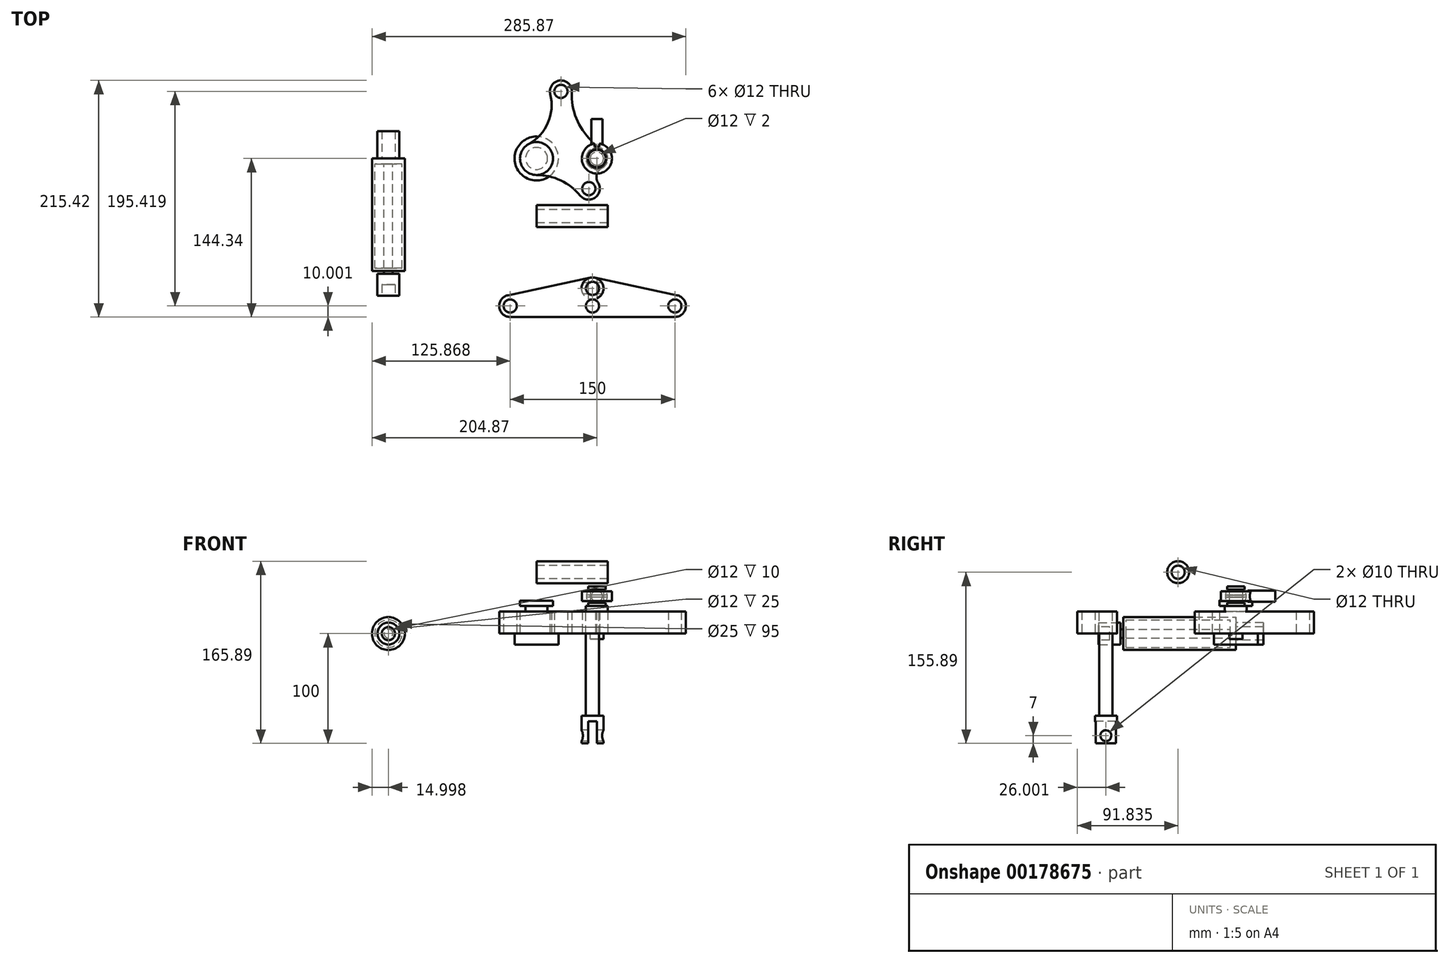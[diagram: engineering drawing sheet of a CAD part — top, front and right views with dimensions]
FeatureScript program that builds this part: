
annotation { "Feature Type Name" : "Feature", "Feature Type Description" : "" }
export const myFeature = defineFeature(function(context is Context, id is Id, definition is map)
    precondition{}
    {
        {
            var Q0;
            Q0=qCreatedBy(makeId("Top.planeOp"),FACE);
            var sketch = newSketch(context, id + "F0", { "sketchPlane" : qUnion([Q0])});
            skCircle(sketch, "E0", {"center": v(0, 0) * mm, "radius": 10 * mm});
            skCircle(sketch, "E1", {"center": v(55, 0) * mm, "radius": 6 * mm});
            skCircle(sketch, "E2", {"center": v(22.23, 61.08) * mm, "radius": 6 * mm});
            skCircle(sketch, "E3", {"center": v(22.23, 61.08) * mm, "radius": 10 * mm});
            skCircle(sketch, "E4", {"center": v(0, 0) * mm, "radius": 15 * mm});
            skCircle(sketch, "E5", {"center": v(55, 0) * mm, "radius": 10 * mm});
            skLineSegment(sketch, "E6", {"start": v(22.23, 61.08) * mm, "end": v(0, 0) * mm, "construction": true});
            skLineSegment(sketch, "E7", {"start": v(0, 0) * mm, "end": v(55, 0) * mm, "construction": true});
            skCircle(sketch, "E8", {"center": v(47.63, -27.5) * mm, "radius": 6 * mm});
            skCircle(sketch, "E9", {"center": v(47.63, -27.5) * mm, "radius": 10 * mm});
            skLineSegment(sketch, "E10", {"start": v(0, 0) * mm, "end": v(47.63, -27.5) * mm, "construction": true});
            skArc(sketch, "E11", {"start": v(-7.24, 13.14) * mm, "mid": v(10.4, 32.52) * mm, "end": v(12.54, 58.63) * mm});
            skArc(sketch, "E12", {"start": v(32.22, 60.57) * mm, "mid": v(38.92, 30.7) * mm, "end": v(60.1, 8.6) * mm});
            skArc(sketch, "E13", {"start": v(39.9, -33.85) * mm, "mid": v(22.07, -19.95) * mm, "end": v(0, -15) * mm});
            skArc(sketch, "E14", {"start": v(59.56, -8.9) * mm, "mid": v(54.87, -14.7) * mm, "end": v(56.03, -22.07) * mm});
            skSolve(sketch);
        }
        {
            var Q0;
            Q0 = qSketchRegion(id + "F0", true);
            extrude(context, id + "F1", {"entities" : qUnion([Q0]), "depth" : 20 * mm});
        }
        {
            var Q0;
            Q0=makeQuery(id+"F1.opExtrude","CAP_FACE",FACE,{"disambiguationData":[OSD([sQuery(id+"F0.wireOp",EDGE,"E0"),sQuery(id+"F0.wireOp",EDGE,"E1"),sQuery(id+"F0.wireOp",EDGE,"E2"),sQuery(id+"F0.wireOp",EDGE,"E3"),sQuery(id+"F0.wireOp",EDGE,"E4"),sQuery(id+"F0.wireOp",EDGE,"E5"),sQuery(id+"F0.wireOp",EDGE,"7eYs1WeX-2swm-OC1l-bZu6-TTdB08adliAf"),sQuery(id+"F0.wireOp",EDGE,"nQsTL9GD-XLsh-tJj3-fAuQ-5O212QxCRfNk"),sQuery(id+"F0.wireOp",EDGE,"hc34mphg-32rM-w2y4-HKMr-pzHpQo0iNHix")])],"isStart":true});
            var sketch = newSketch(context, id + "F2", { "sketchPlane" : qUnion([Q0])});
            skCircle(sketch, "E15", {"center": v(0, 0) * mm, "radius": 20 * mm});
            skSolve(sketch);
        }
        {
            var Q0;
            Q0 = qSketchRegion(id + "F2", true);
            extrude(context, id + "F3", {"entities" : qUnion([Q0]), "depth" : 10 * mm});
        }
        {
            var Q0;
            Q0=makeQuery(id+"F3.opExtrude","CAP_FACE",FACE,{"disambiguationData":[OSD([sQuery(id+"F2.wireOp",EDGE,"E15")])],"isStart":true});
            var sketch = newSketch(context, id + "F4", { "sketchPlane" : qUnion([Q0])});
            skCircle(sketch, "E16", {"center": v(0, 0) * mm, "radius": 10 * mm});
            skSolve(sketch);
        }
        {
            var Q0;
            Q0 = qSketchRegion(id + "F4", true);
            extrude(context, id + "F5", {"entities" : qUnion([Q0]), "operationType" : NewBodyOperationType.ADD, "depth" : 25 * mm});
        }
        {
            var Q0;
            Q0=makeQuery(id+"F5.opExtrude","CAP_FACE",FACE,{"disambiguationData":[OSD([sQuery(id+"F4.wireOp",EDGE,"E16")])],"isStart":false});
            var sketch = newSketch(context, id + "F6", { "sketchPlane" : qUnion([Q0])});
            skCircle(sketch, "E17", {"center": v(0, 0) * mm, "radius": 15 * mm});
            skSolve(sketch);
        }
        {
            var Q0;
            Q0 = qSketchRegion(id + "F6", true);
            extrude(context, id + "F7", {"entities" : qUnion([Q0]), "operationType" : NewBodyOperationType.ADD, "depth" : 5 * mm});
        }
        {
            var Q0;
            Q0=makeQuery(id+"F1.opExtrude","CAP_FACE",FACE,{"disambiguationData":[OSD([sQuery(id+"F0.wireOp",EDGE,"E0"),sQuery(id+"F0.wireOp",EDGE,"E1"),sQuery(id+"F0.wireOp",EDGE,"E2"),sQuery(id+"F0.wireOp",EDGE,"E3"),sQuery(id+"F0.wireOp",EDGE,"E4"),sQuery(id+"F0.wireOp",EDGE,"E5"),sQuery(id+"F0.wireOp",EDGE,"7eYs1WeX-2swm-OC1l-bZu6-TTdB08adliAf"),sQuery(id+"F0.wireOp",EDGE,"nQsTL9GD-XLsh-tJj3-fAuQ-5O212QxCRfNk"),sQuery(id+"F0.wireOp",EDGE,"hc34mphg-32rM-w2y4-HKMr-pzHpQo0iNHix")])],"isStart":false});
            var sketch = newSketch(context, id + "F8", { "sketchPlane" : qUnion([Q0])});
            skCircle(sketch, "E18", {"center": v(55, 0) * mm, "radius": 10 * mm});
            skSolve(sketch);
        }
        {
            var Q0;
            Q0 = qSketchRegion(id + "F8", true);
            extrude(context, id + "F9", {"entities" : qUnion([Q0]), "depth" : 5 * mm});
        }
        {
            var Q0;
            Q0=makeQuery(id+"F9.opExtrude","CAP_FACE",FACE,{"disambiguationData":[OSD([sQuery(id+"F8.wireOp",EDGE,"E18")])],"isStart":false});
            var sketch = newSketch(context, id + "F10", { "sketchPlane" : qUnion([Q0])});
            skCircle(sketch, "E19", {"center": v(55, 0) * mm, "radius": 8 * mm});
            skSolve(sketch);
        }
        {
            var Q0;
            Q0 = qSketchRegion(id + "F10", true);
            extrude(context, id + "F11", {"entities" : qUnion([Q0]), "operationType" : NewBodyOperationType.ADD, "depth" : 3 * mm});
        }
        {
            var Q0;
            Q0=makeQuery(id+"F11.opExtrude","CAP_FACE",FACE,{"disambiguationData":[OSD([sQuery(id+"F10.wireOp",EDGE,"E19")])],"isStart":false});
            var sketch = newSketch(context, id + "F12", { "sketchPlane" : qUnion([Q0])});
            skCircle(sketch, "E20", {"center": v(55, 0) * mm, "radius": 6 * mm});
            skSolve(sketch);
        }
        {
            var Q0;
            Q0 = qSketchRegion(id + "F12", true);
            extrude(context, id + "F13", {"entities" : qUnion([Q0]), "operationType" : NewBodyOperationType.ADD, "depth" : 12 * mm});
        }
        {
            var Q0;
            Q0=makeQuery(id+"F13.opExtrude","CAP_FACE",FACE,{"disambiguationData":[OSD([sQuery(id+"F12.wireOp",EDGE,"E20")])],"isStart":false});
            var sketch = newSketch(context, id + "F14", { "sketchPlane" : qUnion([Q0])});
            skCircle(sketch, "E21", {"center": v(55, 0) * mm, "radius": 8 * mm});
            skSolve(sketch);
        }
        {
            var Q0;
            Q0 = qSketchRegion(id + "F14", true);
            extrude(context, id + "F15", {"entities" : qUnion([Q0]), "operationType" : NewBodyOperationType.ADD, "depth" : 3 * mm});
        }
        {
            var Q0;
            Q0=makeQuery(id+"F9.opExtrude","CAP_FACE",FACE,{"disambiguationData":[OSD([sQuery(id+"F8.wireOp",EDGE,"E18")])],"isStart":true});
            var sketch = newSketch(context, id + "F16", { "sketchPlane" : qUnion([Q0])});
            skCircle(sketch, "E22", {"center": v(55, 0) * mm, "radius": 6 * mm});
            skSolve(sketch);
        }
        {
            var Q0;
            Q0 = qSketchRegion(id + "F16", true);
            extrude(context, id + "F17", {"entities" : qUnion([Q0]), "operationType" : NewBodyOperationType.ADD, "depth" : 25 * mm});
        }
        {
            var Q0;
            Q0=qCreatedBy(makeId("Front.planeOp"),FACE);
            var sketch = newSketch(context, id + "F18", { "sketchPlane" : qUnion([Q0])});
            skLineSegment(sketch, "E23.0", {"start": v(47, 28) * mm, "end": v(63, 28) * mm, "construction": true});
            skLineSegment(sketch, "E24.0", {"start": v(47, 40) * mm, "end": v(63, 40) * mm, "construction": true});
            skLineSegment(sketch, "E25", {"start": v(55, 46.06) * mm, "end": v(55, 21.94) * mm, "construction": true});
            skPoint(sketch, "E25.startSnap0", {"position": v(55, 40) * mm});
            skLineSegment(sketch, "E26", {"start": v(76.42, 34) * mm, "end": v(32.2, 34) * mm, "construction": true});
            skPoint(sketch, "E26.startSnap0", {"position": v(55, 34) * mm});
            skLineSegment(sketch, "E27", {"start": v(61, 35) * mm, "end": v(61, 33) * mm, "construction": true});
            skLineSegment(sketch, "E28", {"start": v(61, 35) * mm, "end": v(64.48, 35) * mm});
            skLineSegment(sketch, "E29", {"start": v(61, 33) * mm, "end": v(64.48, 33) * mm});
            skLineSegment(sketch, "E30", {"start": v(61, 33) * mm, "end": v(61, 35) * mm});
            skArc(sketch, "E31", {"start": v(64.48, 35) * mm, "mid": v(64.53, 34) * mm, "end": v(64.48, 33) * mm});
            skSolve(sketch);
        }
        {
            var Q0;
            Q0 = qSketchRegion(id + "F18", true);
            var Q1;
            Q1=sQuery(id+"F18.wireOp",EDGE,"E25");
            revolve(context, id + "F19", {"entities" : qUnion([Q0]), "axis" : qUnion([Q1]), "revolveType" : RevolveType.FULL});
        }
        {
            var Q0;
            Q0=qCreatedBy(makeId("Front.planeOp"),FACE);
            var sketch = newSketch(context, id + "F20", { "sketchPlane" : qUnion([Q0])});
            skArc(sketch, "E32", {"start": v(48.78, 41.22) * mm, "mid": v(55, 24.47) * mm, "end": v(61.22, 41.22) * mm, "construction": true});
            skLineSegment(sketch, "E33.0", {"start": v(45.52, 33) * mm, "end": v(64.48, 33) * mm, "construction": true});
            skLineSegment(sketch, "E34.0", {"start": v(45.52, 35) * mm, "end": v(64.48, 35) * mm, "construction": true});
            skLineSegment(sketch, "E35", {"start": v(63.4, 38.5) * mm, "end": v(68.73, 38.5) * mm});
            skLineSegment(sketch, "E36", {"start": v(68.73, 38.5) * mm, "end": v(68.73, 29.5) * mm});
            skLineSegment(sketch, "E37", {"start": v(68.73, 29.5) * mm, "end": v(63.4, 29.5) * mm});
            skLineSegment(sketch, "E38", {"start": v(87.4, 34) * mm, "end": v(34.56, 34) * mm, "construction": true});
            skArc(sketch, "E39", {"start": v(63.4, 38.5) * mm, "mid": v(64.53, 34) * mm, "end": v(63.4, 29.5) * mm});
            skLineSegment(sketch, "E40", {"start": v(55, 53.1) * mm, "end": v(55, 13.25) * mm, "construction": true});
            skSolve(sketch);
        }
        {
            var Q0;
            Q0 = qSketchRegion(id + "F20", true);
            var Q1;
            Q1=sQuery(id+"F20.wireOp",EDGE,"E40");
            revolve(context, id + "F21", {"entities" : qUnion([Q0]), "axis" : qUnion([Q1]), "revolveType" : RevolveType.FULL});
        }
        {
            var Q0;
            Q0=qCreatedBy(makeId("Front.planeOp"),FACE);
            cPlane(context, id + "F22", {"entities" : qUnion([Q0]), "cplaneType" : CPlaneType.OFFSET, "offset" : 11 * mm, "oppositeDirection" : true, "width" : 150 * mm, "height" : 150 * mm});
        }
        {
            var Q0;
            Q0=qCreatedBy(id+"F22.planeOp",FACE);
            var sketch = newSketch(context, id + "F23", { "sketchPlane" : qUnion([Q0])});
            skLineSegment(sketch, "E41.0", {"start": v(41.27, 38.5) * mm, "end": v(68.73, 38.5) * mm, "construction": true});
            skLineSegment(sketch, "E42.0", {"start": v(41.27, 29.5) * mm, "end": v(68.73, 29.5) * mm, "construction": true});
            skLineSegment(sketch, "E43", {"start": v(68.73, 43.55) * mm, "end": v(68.73, 34.45) * mm, "construction": true});
            skLineSegment(sketch, "E44", {"start": v(41.27, 34.45) * mm, "end": v(41.27, 43.55) * mm, "construction": true});
            skLineSegment(sketch, "E45", {"start": v(55, 56.1) * mm, "end": v(55, 16.33) * mm, "construction": true});
            skLineSegment(sketch, "E46", {"start": v(74.02, 34) * mm, "end": v(35.67, 34) * mm, "construction": true});
            skCircle(sketch, "E47", {"center": v(55, 34) * mm, "radius": 5 * mm});
            skSolve(sketch);
        }
        {
            var Q0;
            Q0 = qSketchRegion(id + "F23", true);
            extrude(context, id + "F24", {"entities" : qUnion([Q0]), "operationType" : NewBodyOperationType.ADD, "oppositeDirection" : true, "depth" : 25 * mm});
        }
        {
            var Q0;
            Q0=qCreatedBy(makeId("Front.planeOp"),FACE);
            var sketch = newSketch(context, id + "F25", { "sketchPlane" : qUnion([Q0])});
            skCircle(sketch, "E48", {"center": v(-134.87, 0) * mm, "radius": 15 * mm});
            skSolve(sketch);
        }
        {
            var Q0;
            Q0 = qSketchRegion(id + "F25", true);
            extrude(context, id + "F26", {"entities" : qUnion([Q0]), "depth" : 100 * mm});
        }
        {
            var Q0;
            Q0=makeQuery(id+"F26.opExtrude","CAP_FACE",FACE,{"disambiguationData":[OSD([sQuery(id+"F25.wireOp",EDGE,"E48")])],"isStart":false});
            shell(context, id + "F27", {"entities" : qUnion([Q0]), "thickness" : 2.5 * mm});
        }
        {
            var Q0;
            Q0=makeQuery(id+"F26.opExtrude","CAP_FACE",FACE,{"disambiguationData":[OSD([sQuery(id+"F25.wireOp",EDGE,"E48")])],"isStart":false});
            cPlane(context, id + "F28", {"entities" : qUnion([Q0]), "cplaneType" : CPlaneType.OFFSET, "offset" : 100 * mm, "oppositeDirection" : true, "width" : 150 * mm, "height" : 150 * mm});
        }
        {
            var Q0;
            Q0=qCreatedBy(id+"F28.planeOp",FACE);
            var sketch = newSketch(context, id + "F29", { "sketchPlane" : qUnion([Q0])});
            skCircle(sketch, "E49", {"center": v(-134.87, 0) * mm, "radius": 12.5 * mm});
            skSolve(sketch);
        }
        {
            var Q0;
            Q0 = qSketchRegion(id + "F29", true);
            extrude(context, id + "F30", {"entities" : qUnion([Q0]), "depth" : 5 * mm});
        }
        {
            var Q0;
            Q0=makeQuery(id+"F30.opExtrude","CAP_FACE",FACE,{"disambiguationData":[OSD([sQuery(id+"F29.wireOp",EDGE,"E49")])],"isStart":false});
            var sketch = newSketch(context, id + "F31", { "sketchPlane" : qUnion([Q0])});
            skCircle(sketch, "E50", {"center": v(-134.87, 0) * mm, "radius": 4 * mm});
            skSolve(sketch);
        }
        {
            var Q0;
            Q0 = qSketchRegion(id + "F31", true);
            extrude(context, id + "F32", {"entities" : qUnion([Q0]), "operationType" : NewBodyOperationType.ADD, "depth" : 100 * mm});
        }
        {
            var Q0;
            Q0=makeQuery(id+"F26.opExtrude","CAP_FACE",FACE,{"disambiguationData":[OSD([sQuery(id+"F25.wireOp",EDGE,"E48")])],"isStart":false});
            var sketch = newSketch(context, id + "F33", { "sketchPlane" : qUnion([Q0])});
            skCircle(sketch, "E51", {"center": v(-134.87, 0) * mm, "radius": 15 * mm});
            skCircle(sketch, "E52", {"center": v(-134.87, 0) * mm, "radius": 4 * mm});
            skSolve(sketch);
        }
        {
            var Q0;
            Q0 = qSketchRegion(id + "F33", true);
            extrude(context, id + "F34", {"entities" : qUnion([Q0]), "operationType" : NewBodyOperationType.ADD, "depth" : 2.5 * mm});
        }
        {
            var Q0;
            Q0=makeQuery(id+"F32.opExtrude","CAP_FACE",FACE,{"disambiguationData":[OSD([sQuery(id+"F31.wireOp",EDGE,"E50")])],"isStart":false});
            var sketch = newSketch(context, id + "F35", { "sketchPlane" : qUnion([Q0])});
            skCircle(sketch, "E53", {"center": v(-134.87, 0) * mm, "radius": 10 * mm});
            skSolve(sketch);
        }
        {
            var Q0;
            Q0 = qSketchRegion(id + "F35", true);
            extrude(context, id + "F36", {"entities" : qUnion([Q0]), "operationType" : NewBodyOperationType.ADD, "depth" : 20 * mm});
        }
        {
            var Q0;
            Q0=makeQuery(id+"F26.opExtrude","CAP_FACE",FACE,{"disambiguationData":[OSD([sQuery(id+"F25.wireOp",EDGE,"E48")])],"isStart":true});
            var sketch = newSketch(context, id + "F37", { "sketchPlane" : qUnion([Q0])});
            skCircle(sketch, "E54", {"center": v(134.87, 0) * mm, "radius": 10 * mm});
            skCircle(sketch, "E55", {"center": v(134.87, 0) * mm, "radius": 6 * mm});
            skSolve(sketch);
        }
        {
            var Q0;
            Q0=qCreatedBy(makeId("Top.planeOp"),FACE);
            var sketch = newSketch(context, id + "F38", { "sketchPlane" : qUnion([Q0])});
            skCircle(sketch, "E56", {"center": v(51, -134.34) * mm, "radius": 6 * mm});
            skCircle(sketch, "E57", {"center": v(126, -134.34) * mm, "radius": 6 * mm});
            skCircle(sketch, "E58", {"center": v(-24, -134.34) * mm, "radius": 6 * mm});
            skLineSegment(sketch, "E59", {"start": v(51, -58.71) * mm, "end": v(51, -260.51) * mm, "construction": true});
            skLineSegment(sketch, "E60", {"start": v(-69.62, -134.34) * mm, "end": v(303.46, -134.34) * mm, "construction": true});
            skLineSegment(sketch, "E61", {"start": v(303.46, -134.34) * mm, "end": v(303.46, -135.94) * mm, "construction": true});
            skCircle(sketch, "E62", {"center": v(-24, -134.34) * mm, "radius": 10 * mm});
            skCircle(sketch, "E63", {"center": v(126, -134.34) * mm, "radius": 10 * mm});
            skCircle(sketch, "E64", {"center": v(51, -134.34) * mm, "radius": 10 * mm});
            skLineSegment(sketch, "E65", {"start": v(48.91, -108.56) * mm, "end": v(-26.09, -124.56) * mm});
            skLineSegment(sketch, "E66", {"start": v(-24, -144.34) * mm, "end": v(51, -144.34) * mm});
            skLineSegment(sketch, "E67", {"start": v(51, -144.34) * mm, "end": v(126, -144.34) * mm});
            skLineSegment(sketch, "E68", {"start": v(128.08, -124.56) * mm, "end": v(53.08, -108.56) * mm});
            skCircle(sketch, "E69", {"center": v(51, -118.34) * mm, "radius": 6 * mm});
            skCircle(sketch, "E70", {"center": v(51, -118.34) * mm, "radius": 10 * mm});
            skSolve(sketch);
        }
        {
            var Q0;
            Q0 = qSketchRegion(id + "F38", true);
            var Q1;
            {var subQ0=sQuery(id+"F38.wireOp",EDGE,"E64");var subQ1=makeQuery(id+"F38.imprint","INTERSECT",VERTEX,{"derivedFrom":[subQ0,sQuery(id+"F38.wireOp",EDGE,"E69")]});Q1=makeQuery(id+"F38.imprint","IMPRINT",FACE,{"disambiguationData":[TD([[makeQuery(id+"F38.imprint","IMPRINT",EDGE,{"disambiguationData":[TD([[subQ1,1.0]])],"derivedFrom":subQ0}),1.0]])]});}
            extrude(context, id + "F39", {"entities" : qUnion([Q0, Q1]), "depth" : 20 * mm});
        }
        {
            var Q0;
            Q0=makeQuery(id+"F39.opExtrude","CAP_FACE",FACE,{"disambiguationData":[OSD([sQuery(id+"F38.wireOp",EDGE,"E56"),sQuery(id+"F38.wireOp",EDGE,"E57"),sQuery(id+"F38.wireOp",EDGE,"E58"),sQuery(id+"F38.wireOp",EDGE,"E62"),sQuery(id+"F38.wireOp",EDGE,"E63"),sQuery(id+"F38.wireOp",EDGE,"E64"),sQuery(id+"F38.wireOp",EDGE,"E65"),sQuery(id+"F38.wireOp",EDGE,"E66"),sQuery(id+"F38.wireOp",EDGE,"E67"),sQuery(id+"F38.wireOp",EDGE,"E68"),sQuery(id+"F38.wireOp",EDGE,"E69"),sQuery(id+"F38.wireOp",EDGE,"E70")])],"isStart":true});
            var sketch = newSketch(context, id + "F40", { "sketchPlane" : qUnion([Q0])});
            skCircle(sketch, "E71", {"center": v(51, 118.34) * mm, "radius": 6 * mm});
            skSolve(sketch);
        }
        {
            var Q0;
            Q0 = qSketchRegion(id + "F40", true);
            var Q1;
            Q1=makeQuery(id+"F39.opExtrude","CAP_FACE",FACE,{"disambiguationData":[OSD([sQuery(id+"F38.wireOp",EDGE,"E56"),sQuery(id+"F38.wireOp",EDGE,"E57"),sQuery(id+"F38.wireOp",EDGE,"E58"),sQuery(id+"F38.wireOp",EDGE,"E62"),sQuery(id+"F38.wireOp",EDGE,"E63"),sQuery(id+"F38.wireOp",EDGE,"E64"),sQuery(id+"F38.wireOp",EDGE,"E65"),sQuery(id+"F38.wireOp",EDGE,"E66"),sQuery(id+"F38.wireOp",EDGE,"E67"),sQuery(id+"F38.wireOp",EDGE,"E68"),sQuery(id+"F38.wireOp",EDGE,"E69"),sQuery(id+"F38.wireOp",EDGE,"E70")])],"isStart":false});
            extrude(context, id + "F41", {"entities" : qUnion([Q0]), "depth" : 75 * mm, "hasSecondDirection" : true, "secondDirectionBound" : SecondDirectionBoundingType.UP_TO_SURFACE, "secondDirectionOppositeDirection" : true, "secondDirectionBoundEntityFace" : qUnion([Q1]), "secondDirectionDepth" : 25 * mm});
        }
        {
            var Q0;
            Q0=makeQuery(id+"F41.opExtrude","CAP_FACE",FACE,{"disambiguationData":[OSD([sQuery(id+"F40.wireOp",EDGE,"E71")])],"isStart":false});
            var sketch = newSketch(context, id + "F42", { "sketchPlane" : qUnion([Q0])});
            skCircle(sketch, "E72", {"center": v(51, 118.34) * mm, "radius": 10 * mm});
            skSolve(sketch);
        }
        {
            var Q0;
            Q0 = qSketchRegion(id + "F42", true);
            extrude(context, id + "F43", {"entities" : qUnion([Q0]), "operationType" : NewBodyOperationType.ADD, "depth" : 25 * mm});
        }
        {
            var Q0;
            Q0=makeQuery(id+"F43.opExtrude","CAP_FACE",FACE,{"disambiguationData":[OSD([sQuery(id+"F42.wireOp",EDGE,"E72")])],"isStart":false});
            var sketch = newSketch(context, id + "F44", { "sketchPlane" : qUnion([Q0])});
            skLineSegment(sketch, "E73.bottom", {"start": v(47, 104.3) * mm, "end": v(55, 104.3) * mm});
            skLineSegment(sketch, "E73.top", {"start": v(47, 132.38) * mm, "end": v(55, 132.38) * mm});
            skLineSegment(sketch, "E73.left", {"start": v(47, 104.3) * mm, "end": v(47, 132.38) * mm});
            skLineSegment(sketch, "E73.right", {"start": v(55, 104.3) * mm, "end": v(55, 132.38) * mm});
            skPoint(sketch, "E73.middle", {"position": v(51, 118.34) * mm});
            skSolve(sketch);
        }
        {
            var Q0;
            Q0 = qSketchRegion(id + "F44", true);
            extrude(context, id + "F45", {"entities" : qUnion([Q0]), "operationType" : NewBodyOperationType.REMOVE, "oppositeDirection" : true, "depth" : 20 * mm});
        }
        {
            var Q0;
            Q0=makeQuery(id+"F45.boolean.opBoolean","COPY",FACE,{"derivedFrom":makeQuery(id+"F45.opExtrude","SWEPT_FACE",FACE,{"disambiguationData":[OSD([sQuery(id+"F44.wireOp",EDGE,"E73.right")])]})});
            var sketch = newSketch(context, id + "F46", { "sketchPlane" : qUnion([Q0])});
            skCircle(sketch, "E74", {"center": v(118.34, -93) * mm, "radius": 5 * mm});
            skPoint(sketch, "E74.centerSnap0", {"position": v(118.34, -80) * mm});
            skSolve(sketch);
        }
        {
            var Q0;
            Q0 = qSketchRegion(id + "F46", true);
            extrude(context, id + "F47", {"entities" : qUnion([Q0]), "operationType" : NewBodyOperationType.REMOVE, "endBound" : BoundingType.THROUGH_ALL, "oppositeDirection" : true, "depth" : 25 * mm, "hasSecondDirection" : true, "secondDirectionBound" : SecondDirectionBoundingType.THROUGH_ALL, "secondDirectionOppositeDirection" : false, "secondDirectionDepth" : 25 * mm});
        }
        {
            var Q0;
            Q0=makeQuery(id+"F36.opExtrude","CAP_FACE",FACE,{"disambiguationData":[OSD([sQuery(id+"F35.wireOp",EDGE,"E53")])],"isStart":false});
            var sketch = newSketch(context, id + "F48", { "sketchPlane" : qUnion([Q0])});
            skCircle(sketch, "E75", {"center": v(-134.87, 0) * mm, "radius": 6 * mm});
            skSolve(sketch);
        }
        {
            var Q0;
            Q0 = qSketchRegion(id + "F48", true);
            extrude(context, id + "F49", {"entities" : qUnion([Q0]), "operationType" : NewBodyOperationType.REMOVE, "oppositeDirection" : true, "depth" : 10 * mm});
        }
        {
            var Q0;
            Q0 = qSketchRegion(id + "F37", true);
            extrude(context, id + "F50", {"entities" : qUnion([Q0]), "operationType" : NewBodyOperationType.ADD, "depth" : 25 * mm});
        }
        {
            var Q0;
            Q0=qCreatedBy(makeId("Right.planeOp"),FACE);
            var sketch = newSketch(context, id + "F51", { "sketchPlane" : qUnion([Q0])});
            skCircle(sketch, "E76", {"center": v(-52.5, 55.89) * mm, "radius": 10 * mm});
            skCircle(sketch, "E77", {"center": v(-52.5, 55.89) * mm, "radius": 6 * mm});
            skSolve(sketch);
        }
        {
            var Q0;
            Q0 = qSketchRegion(id + "F51", true);
            extrude(context, id + "F52", {"entities" : qUnion([Q0]), "depth" : 65 * mm});
        }
    });
